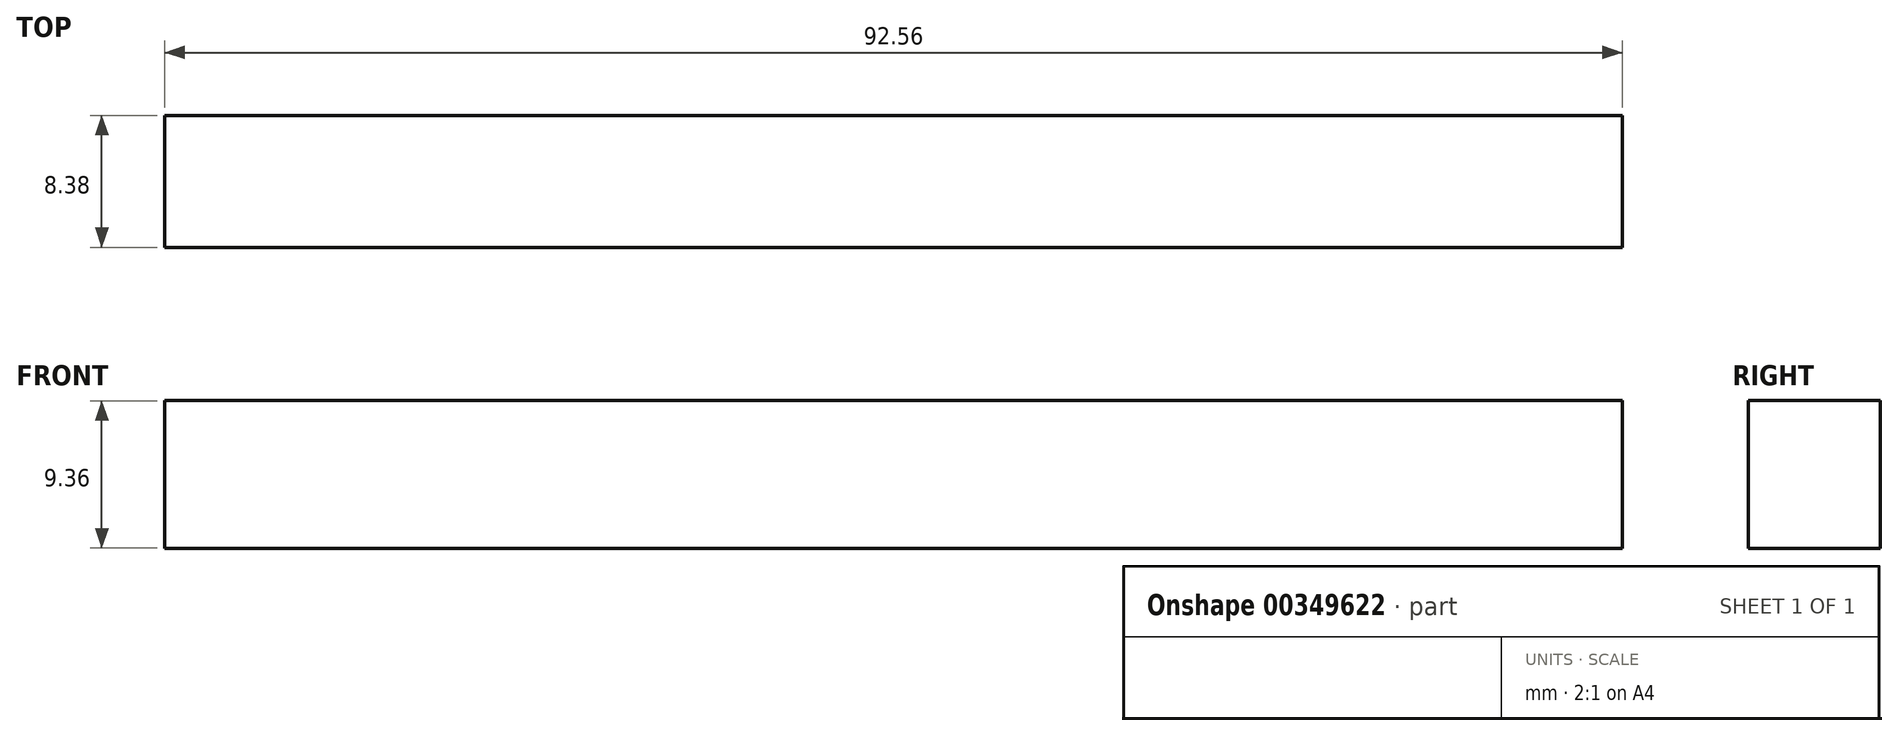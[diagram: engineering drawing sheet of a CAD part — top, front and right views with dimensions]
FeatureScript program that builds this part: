
annotation { "Feature Type Name" : "Feature", "Feature Type Description" : "" }
export const myFeature = defineFeature(function(context is Context, id is Id, definition is map)
    precondition{}
    {
        {
            var Q0;
            Q0=qCreatedBy(makeId("Front.planeOp"),FACE);
            var sketch = newSketch(context, id + "F0", { "sketchPlane" : qUnion([Q0])});
            skLineSegment(sketch, "E0.bottom", {"start": v(46.28, -4.68) * mm, "end": v(-46.28, -4.68) * mm});
            skLineSegment(sketch, "E0.top", {"start": v(46.28, 4.68) * mm, "end": v(-46.28, 4.68) * mm});
            skLineSegment(sketch, "E0.left", {"start": v(46.28, -4.68) * mm, "end": v(46.28, 4.68) * mm});
            skLineSegment(sketch, "E0.right", {"start": v(-46.28, -4.68) * mm, "end": v(-46.28, 4.68) * mm});
            skPoint(sketch, "E0.middle", {"position": v(0, 0) * mm});
            skSolve(sketch);
        }
        {
            var Q0;
            Q0 = qSketchRegion(id + "F0", true);
            extrude(context, id + "F1", {"entities" : qUnion([Q0]), "oppositeDirection" : true, "depth" : 8.38 * mm});
        }
    });
